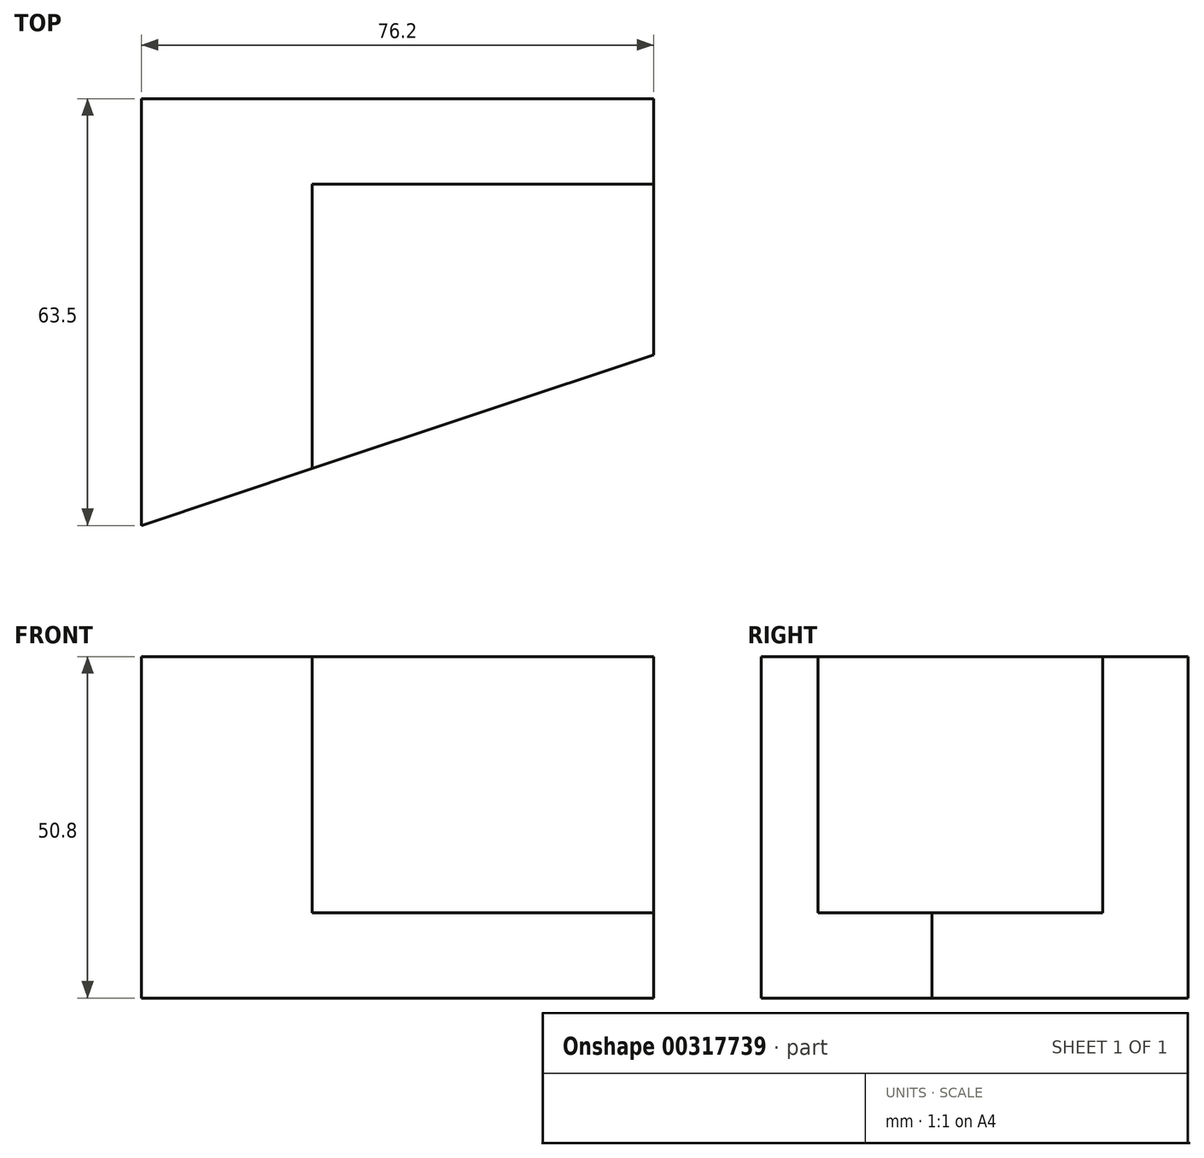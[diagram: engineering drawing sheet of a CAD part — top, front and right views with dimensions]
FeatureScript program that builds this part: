
annotation { "Feature Type Name" : "Feature", "Feature Type Description" : "" }
export const myFeature = defineFeature(function(context is Context, id is Id, definition is map)
    precondition{}
    {
        {
            var Q0;
            Q0=qCreatedBy(makeId("Front.planeOp"),FACE);
            var sketch = newSketch(context, id + "F0", { "sketchPlane" : qUnion([Q0])});
            skLineSegment(sketch, "E0.bottom", {"start": v(0, 0) * mm, "end": v(76.2, 0) * mm});
            skLineSegment(sketch, "E0.top", {"start": v(0, 50.8) * mm, "end": v(25.4, 50.8) * mm});
            skLineSegment(sketch, "E0.left", {"start": v(0, 0) * mm, "end": v(0, 50.8) * mm});
            skLineSegment(sketch, "E0.right", {"start": v(76.2, 0) * mm, "end": v(76.2, 12.7) * mm});
            skLineSegment(sketch, "E1.top", {"start": v(76.2, 12.7) * mm, "end": v(25.4, 12.7) * mm});
            skLineSegment(sketch, "E1.right", {"start": v(25.4, 50.8) * mm, "end": v(25.4, 12.7) * mm});
            skSolve(sketch);
        }
        {
            var Q0;
            Q0 = qSketchRegion(id + "F0", true);
            extrude(context, id + "F1", {"entities" : qUnion([Q0]), "depth" : 63.5 * mm});
        }
        {
            var Q0;
            Q0=makeQuery(id+"F1.opExtrude","SWEPT_FACE",FACE,{"disambiguationData":[OSD([sQuery(id+"F0.wireOp",EDGE,"E1.right")])]});
            var sketch = newSketch(context, id + "F2", { "sketchPlane" : qUnion([Q0])});
            skLineSegment(sketch, "E2.bottom", {"start": v(0, 50.8) * mm, "end": v(-12.7, 50.8) * mm});
            skLineSegment(sketch, "E2.top", {"start": v(0, 12.7) * mm, "end": v(-12.7, 12.7) * mm});
            skLineSegment(sketch, "E2.left", {"start": v(0, 50.8) * mm, "end": v(0, 12.7) * mm});
            skLineSegment(sketch, "E2.right", {"start": v(-12.7, 50.8) * mm, "end": v(-12.7, 12.7) * mm});
            skSolve(sketch);
        }
        {
            var Q0;
            Q0 = qSketchRegion(id + "F2", true);
            var Q1;
            Q1=makeQuery(id+"F1.opExtrude","SWEPT_FACE",FACE,{"disambiguationData":[OSD([sQuery(id+"F0.wireOp",EDGE,"E0.right")])]});
            extrude(context, id + "F3", {"entities" : qUnion([Q0]), "operationType" : NewBodyOperationType.ADD, "endBound" : BoundingType.UP_TO_SURFACE, "endBoundEntityFace" : qUnion([Q1]), "depth" : 25.4 * mm});
        }
        {
            var Q0;
            Q0=makeQuery(id+"F1.opExtrude","SWEPT_FACE",FACE,{"disambiguationData":[OSD([sQuery(id+"F0.wireOp",EDGE,"E1.top")])]});
            var sketch = newSketch(context, id + "F4", { "sketchPlane" : qUnion([Q0])});
            skPoint(sketch, "E3", {"position": v(76.2, -38.1) * mm});
            skLineSegment(sketch, "E4", {"start": v(76.2, -38.1) * mm, "end": v(0, -63.5) * mm});
            skSolve(sketch);
        }
        {
            var Q0;
            {var subQ1=sQuery(id+"F0.wireOp",EDGE,"E1.top");var subQ6=makeQuery(id+"F1.opExtrude","CAP_EDGE",EDGE,{"disambiguationData":[OSD([subQ1])],"isStart":false});Q0=makeQuery(id+"F4.imprint","IMPRINT",FACE,{"disambiguationData":[TD([[makeQuery(id+"F4.imprint","IMPRINT",EDGE,{"derivedFrom":subQ6}),-1.0]])]});}
            extrude(context, id + "F5", {"entities" : qUnion([Q0]), "operationType" : NewBodyOperationType.REMOVE, "endBound" : BoundingType.THROUGH_ALL, "oppositeDirection" : true, "depth" : 25.4 * mm});
        }
        {
            var Q0;
            Q0=makeQuery(id+"F3.boolean.opBoolean","MERGE",FACE,{"derivedFrom":[makeQuery(id+"F1.opExtrude","SWEPT_FACE",FACE,{"disambiguationData":[OSD([sQuery(id+"F0.wireOp",EDGE,"E0.top")])]}),makeQuery(id+"F3.opExtrude","SWEPT_FACE",FACE,{"disambiguationData":[OSD([sQuery(id+"F2.wireOp",EDGE,"E2.bottom")])]})]});
            var sketch = newSketch(context, id + "F6", { "sketchPlane" : qUnion([Q0])});
            skPoint(sketch, "E5", {"position": v(25.4, -55.03) * mm});
            skLineSegment(sketch, "E6", {"start": v(25.4, -55.03) * mm, "end": v(0, -63.5) * mm});
            skSolve(sketch);
        }
        {
            var Q0;
            {var subQ0=sQuery(id+"F6.wireOp",EDGE,"E6");Q0=makeQuery(id+"F6.imprint","IMPRINT",FACE,{"disambiguationData":[TD([[makeQuery(id+"F6.imprint","IMPRINT",EDGE,{"derivedFrom":subQ0}),1.0]])]});}
            extrude(context, id + "F7", {"entities" : qUnion([Q0]), "operationType" : NewBodyOperationType.REMOVE, "endBound" : BoundingType.THROUGH_ALL, "oppositeDirection" : true, "depth" : 25.4 * mm});
        }
    });
